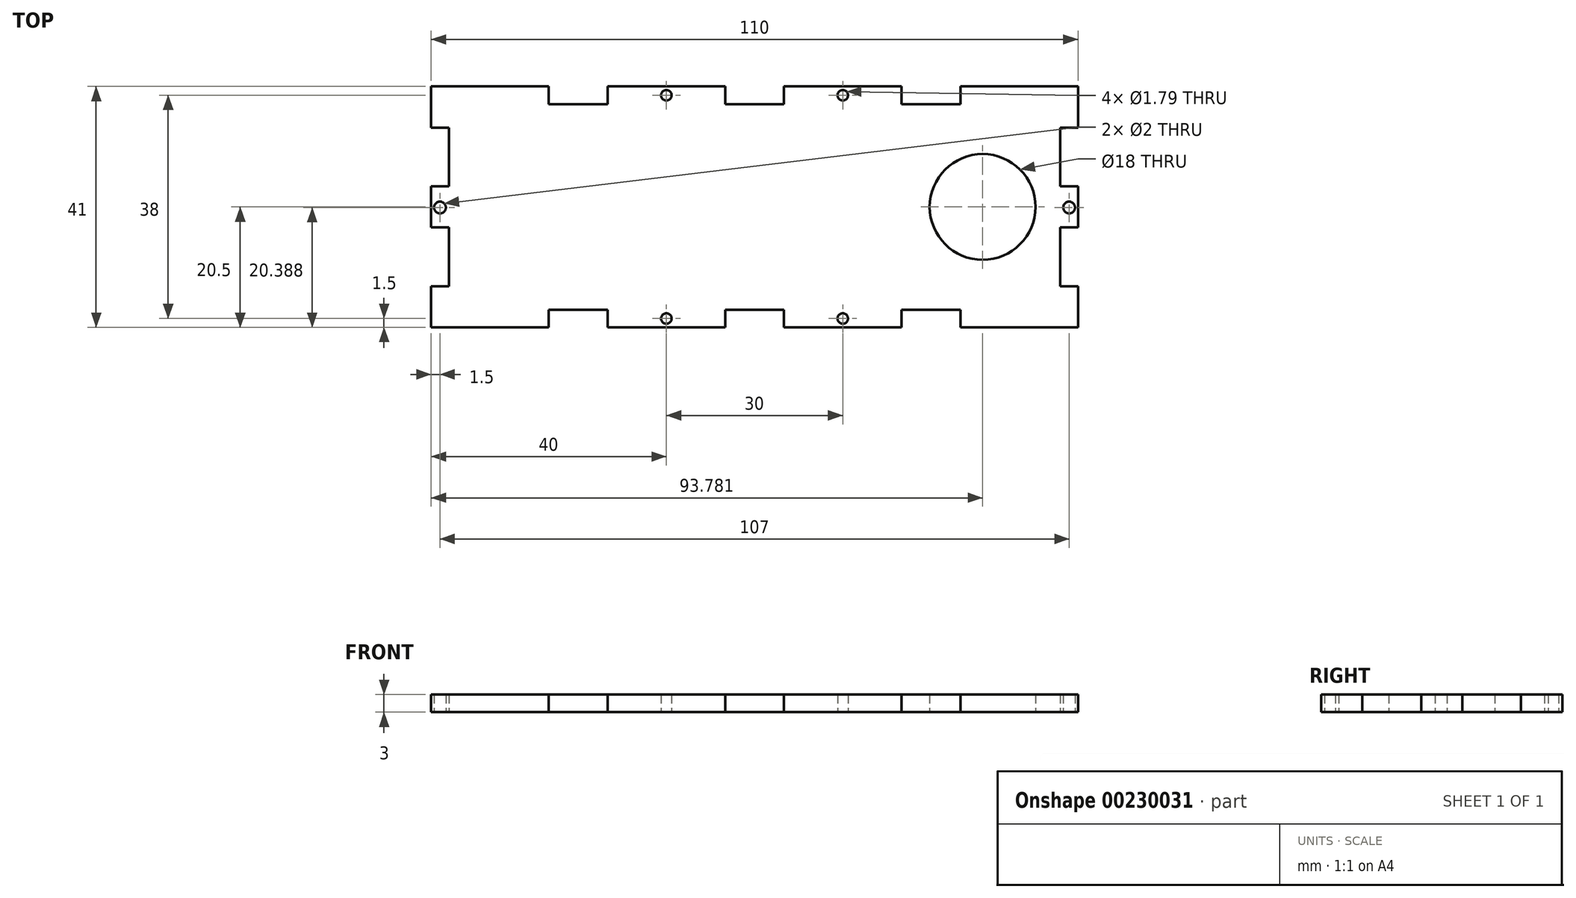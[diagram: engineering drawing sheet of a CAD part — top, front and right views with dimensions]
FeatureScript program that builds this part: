
annotation { "Feature Type Name" : "Feature", "Feature Type Description" : "" }
export const myFeature = defineFeature(function(context is Context, id is Id, definition is map)
    precondition{}
    {
        {
            var Q0;
            Q0=qCreatedBy(makeId("Top.planeOp"),FACE);
            var sketch = newSketch(context, id + "F0", { "sketchPlane" : qUnion([Q0])});
            skLineSegment(sketch, "E0", {"start": v(0, 0) * mm, "end": v(0, 7) * mm});
            skLineSegment(sketch, "E1", {"start": v(0, 7) * mm, "end": v(3, 7) * mm});
            skLineSegment(sketch, "E2", {"start": v(3, 7) * mm, "end": v(3, 17) * mm});
            skLineSegment(sketch, "E3", {"start": v(3, 17) * mm, "end": v(0, 17) * mm});
            skLineSegment(sketch, "E4", {"start": v(0, 17) * mm, "end": v(0, 24) * mm});
            skLineSegment(sketch, "E5", {"start": v(0, 24) * mm, "end": v(3, 24) * mm});
            skLineSegment(sketch, "E6", {"start": v(3, 24) * mm, "end": v(3, 34) * mm});
            skLineSegment(sketch, "E7", {"start": v(3, 34) * mm, "end": v(0, 34) * mm});
            skLineSegment(sketch, "E8", {"start": v(0, 34) * mm, "end": v(0, 41) * mm});
            skLineSegment(sketch, "E9", {"start": v(0, 41) * mm, "end": v(20, 41) * mm});
            skLineSegment(sketch, "E10", {"start": v(20, 41) * mm, "end": v(20, 38) * mm});
            skLineSegment(sketch, "E11", {"start": v(20, 38) * mm, "end": v(30, 38) * mm});
            skLineSegment(sketch, "E12", {"start": v(30, 38) * mm, "end": v(30, 41) * mm});
            skLineSegment(sketch, "E13", {"start": v(30, 41) * mm, "end": v(50, 41) * mm});
            skLineSegment(sketch, "E14", {"start": v(50, 41) * mm, "end": v(50, 38) * mm});
            skLineSegment(sketch, "E15", {"start": v(50, 38) * mm, "end": v(55, 38) * mm});
            skLineSegment(sketch, "E16", {"start": v(55, 41) * mm, "end": v(55, 0) * mm, "construction": true});
            skLineSegment(sketch, "E17", {"start": v(0, 20.5) * mm, "end": v(55, 20.5) * mm, "construction": true});
            skLineSegment(sketch, "E18.MirrorCS", {"start": v(20, 0) * mm, "end": v(20, 3) * mm});
            skLineSegment(sketch, "E19.MirrorCS", {"start": v(30, 3) * mm, "end": v(30, 0) * mm});
            skLineSegment(sketch, "E20.MirrorCS", {"start": v(50, 0) * mm, "end": v(50, 3) * mm});
            skLineSegment(sketch, "E21.MirrorCS", {"start": v(30, 0) * mm, "end": v(50, 0) * mm});
            skLineSegment(sketch, "E22.MirrorCS", {"start": v(20, 3) * mm, "end": v(30, 3) * mm});
            skLineSegment(sketch, "E23.MirrorCS", {"start": v(50, 3) * mm, "end": v(55, 3) * mm});
            skLineSegment(sketch, "E24.MirrorCS", {"start": v(0, 0) * mm, "end": v(20, 0) * mm});
            skLineSegment(sketch, "E25.MirrorCS", {"start": v(90, 41) * mm, "end": v(90, 38) * mm});
            skLineSegment(sketch, "E26.MirrorCS", {"start": v(80, 38) * mm, "end": v(80, 41) * mm});
            skLineSegment(sketch, "E27.MirrorCS", {"start": v(107, 34) * mm, "end": v(110, 34) * mm});
            skLineSegment(sketch, "E28.MirrorCS", {"start": v(110, 24) * mm, "end": v(107, 24) * mm});
            skLineSegment(sketch, "E29.MirrorCS", {"start": v(60, 41) * mm, "end": v(60, 38) * mm});
            skLineSegment(sketch, "E30.MirrorCS", {"start": v(80, 3) * mm, "end": v(80, 0) * mm});
            skLineSegment(sketch, "E31.MirrorCS", {"start": v(110, 7) * mm, "end": v(107, 7) * mm});
            skLineSegment(sketch, "E32.MirrorCS", {"start": v(90, 0) * mm, "end": v(90, 3) * mm});
            skLineSegment(sketch, "E33.MirrorCS", {"start": v(60, 0) * mm, "end": v(60, 3) * mm});
            skLineSegment(sketch, "E34.MirrorCS", {"start": v(107, 17) * mm, "end": v(110, 17) * mm});
            skLineSegment(sketch, "E35.MirrorCS", {"start": v(110, 17) * mm, "end": v(110, 24) * mm});
            skLineSegment(sketch, "E36.MirrorCS", {"start": v(60, 3) * mm, "end": v(55, 3) * mm});
            skLineSegment(sketch, "E37.MirrorCS", {"start": v(110, 41) * mm, "end": v(90, 41) * mm});
            skLineSegment(sketch, "E38.MirrorCS", {"start": v(80, 0) * mm, "end": v(60, 0) * mm});
            skLineSegment(sketch, "E39.MirrorCS", {"start": v(90, 38) * mm, "end": v(80, 38) * mm});
            skLineSegment(sketch, "E40.MirrorCS", {"start": v(80, 41) * mm, "end": v(60, 41) * mm});
            skLineSegment(sketch, "E41.MirrorCS", {"start": v(107, 24) * mm, "end": v(107, 34) * mm});
            skLineSegment(sketch, "E42.MirrorCS", {"start": v(110, 0) * mm, "end": v(90, 0) * mm});
            skLineSegment(sketch, "E43.MirrorCS", {"start": v(60, 38) * mm, "end": v(55, 38) * mm});
            skLineSegment(sketch, "E44.MirrorCS", {"start": v(107, 7) * mm, "end": v(107, 17) * mm});
            skLineSegment(sketch, "E45.MirrorCS", {"start": v(90, 3) * mm, "end": v(80, 3) * mm});
            skLineSegment(sketch, "E46.MirrorCS", {"start": v(110, 20.5) * mm, "end": v(55, 20.5) * mm, "construction": true});
            skLineSegment(sketch, "E47.MirrorCS", {"start": v(110, 34) * mm, "end": v(110, 41) * mm});
            skLineSegment(sketch, "E48.MirrorCS", {"start": v(110, 0) * mm, "end": v(110, 7) * mm});
            skCircle(sketch, "E49", {"center": v(1.5, 20.39) * mm, "radius": 1 * mm});
            skCircle(sketch, "E50", {"center": v(40, 39.5) * mm, "radius": 0.9 * mm});
            skCircle(sketch, "E51.MirrorC", {"center": v(40, 1.5) * mm, "radius": 0.9 * mm});
            skCircle(sketch, "E52.MirrorC", {"center": v(108.5, 20.39) * mm, "radius": 1 * mm});
            skLineSegment(sketch, "E53.MirrorCS", {"start": v(55, 0) * mm, "end": v(55, 41) * mm, "construction": true});
            skCircle(sketch, "E54.MirrorC", {"center": v(70, 39.5) * mm, "radius": 0.9 * mm});
            skCircle(sketch, "E55.MirrorC", {"center": v(70, 1.5) * mm, "radius": 0.9 * mm});
            skCircle(sketch, "E56", {"center": v(93.78, 20.5) * mm, "radius": 9 * mm});
            skSolve(sketch);
        }
        {
            var Q0;
            Q0 = qSketchRegion(id + "F0", true);
            extrude(context, id + "F1", {"entities" : qUnion([Q0]), "depth" : 3 * mm});
        }
    });
